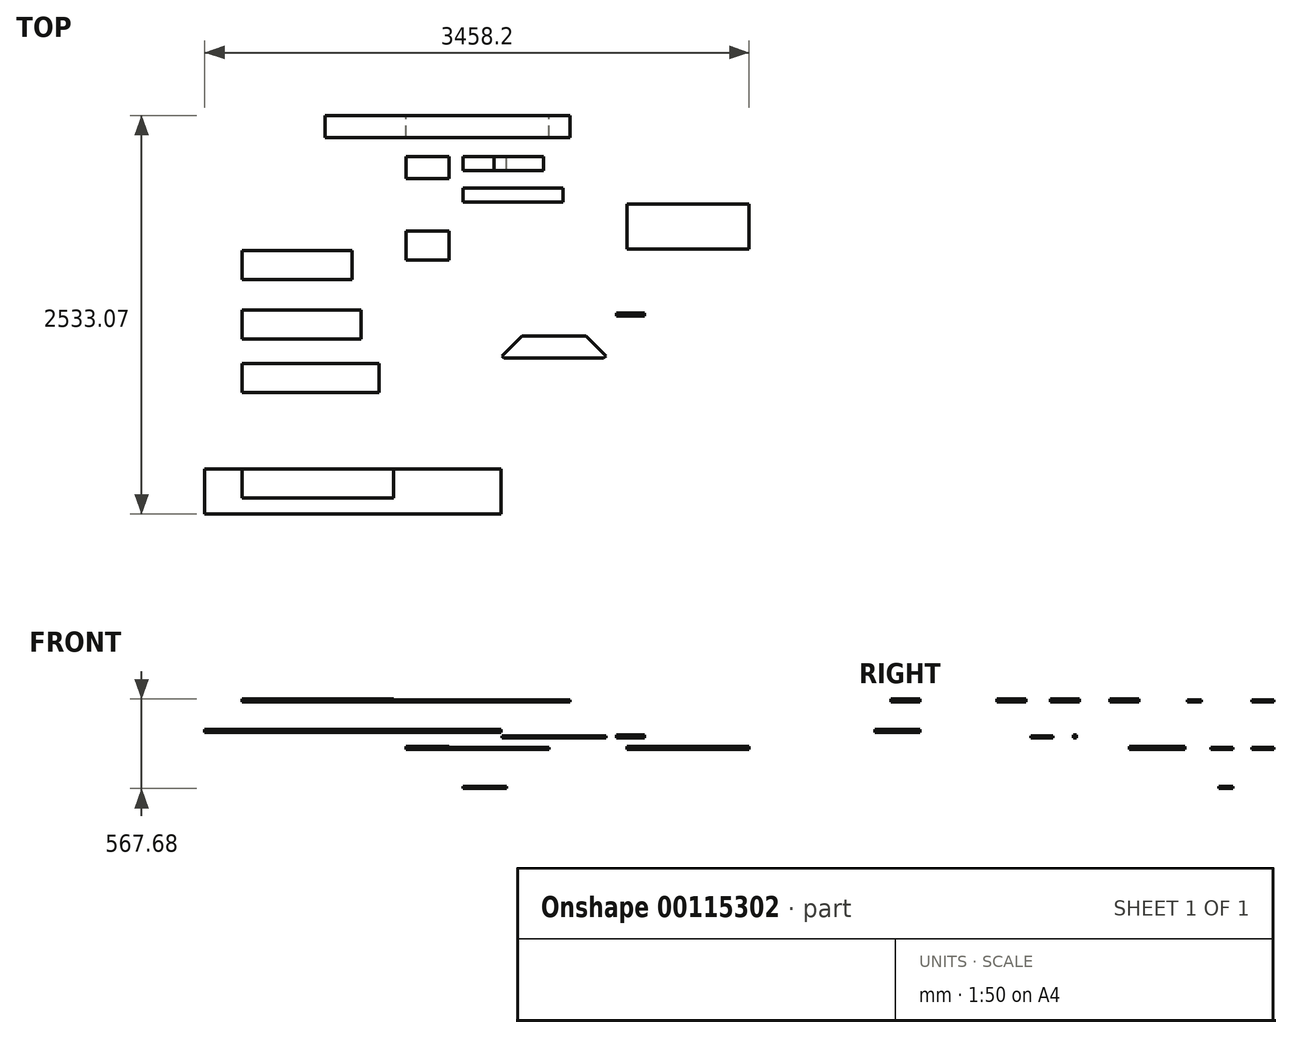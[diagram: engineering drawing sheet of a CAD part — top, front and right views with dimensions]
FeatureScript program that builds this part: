
annotation { "Feature Type Name" : "Feature", "Feature Type Description" : "" }
export const myFeature = defineFeature(function(context is Context, id is Id, definition is map)
    precondition{}
    {
        {
            var Q0;
            Q0=qCreatedBy(makeId("Right.planeOp"),FACE);
            var sketch = newSketch(context, id + "F0", { "sketchPlane" : qUnion([Q0])});
            skLineSegment(sketch, "E0.bottom", {"start": v(-154.99, 55.8) * mm, "end": v(29.16, 55.8) * mm});
            skLineSegment(sketch, "E0.top", {"start": v(-154.99, 36.74) * mm, "end": v(29.16, 36.74) * mm});
            skLineSegment(sketch, "E0.left", {"start": v(-154.99, 55.8) * mm, "end": v(-154.99, 36.74) * mm});
            skLineSegment(sketch, "E0.right", {"start": v(29.16, 55.8) * mm, "end": v(29.16, 36.74) * mm});
            skSolve(sketch);
        }
        {
            var Q0;
            Q0=makeQuery(id+"F0.imprint","IMPRINT",FACE,{"disambiguationData":[TD([[makeQuery(id+"F0.imprint","IMPRINT",EDGE,{"derivedFrom":sQuery(id+"F0.wireOp",EDGE,"E0.bottom")}),-1.0]])]});
            extrude(context, id + "F1", {"entities" : qUnion([Q0]), "depth" : 965.2 * mm});
        }
        {
            var Q0;
            Q0=makeQuery(id+"F1.opExtrude","SWEPT_BODY",BODY,{"disambiguationData":[OSD([sQuery(id+"F0.wireOp",EDGE,"E0.bottom"),sQuery(id+"F0.wireOp",EDGE,"E0.top"),sQuery(id+"F0.wireOp",EDGE,"E0.left"),sQuery(id+"F0.wireOp",EDGE,"E0.right")])]});
            transform(context, id + "F2", {"entities" : qUnion([Q0]), "transformType" : TransformType.TRANSLATION_3D, "dx" : 311.4 * mm, "dy" : 0 * mm, "dz" : 190.77 * mm, "makeCopy" : true});
        }
        {
            var Q0;
            Q0=makeQuery(id+"F1.opExtrude","SWEPT_FACE",FACE,{"disambiguationData":[OSD([sQuery(id+"F0.wireOp",EDGE,"E0.left")])]});
            extrude(context, id + "F3", {"entities" : qUnion([Q0]), "operationType" : NewBodyOperationType.ADD, "depth" : 69.85 * mm});
        }
        {
            var Q0;
            Q0=makeQuery(id+"F3.opExtrude","CAP_FACE",FACE,{"disambiguationData":[OSD([sQuery(id+"F0.wireOp",EDGE,"E0.left")])],"isStart":false});
            extrude(context, id + "F4", {"entities" : qUnion([Q0]), "operationType" : NewBodyOperationType.ADD, "depth" : 31.75 * mm});
        }
        {
            var Q0;
            {var subQ0=sQuery(id+"F0.wireOp",EDGE,"E0.left");var subQ1=makeQuery(id+"F1.opExtrude","CAP_EDGE",EDGE,{"disambiguationData":[OSD([subQ0])],"isStart":false});Q0=makeQuery(id+"F4.boolean.opBoolean","MERGE",FACE,{"derivedFrom":[makeQuery(id+"F3.boolean.opBoolean","MERGE",FACE,{"derivedFrom":[makeQuery(id+"F1.opExtrude","CAP_FACE",FACE,{"disambiguationData":[OSD([sQuery(id+"F0.wireOp",EDGE,"E0.bottom"),sQuery(id+"F0.wireOp",EDGE,"E0.top"),subQ0,sQuery(id+"F0.wireOp",EDGE,"E0.right")])],"isStart":false}),makeQuery(id+"F3.opExtrude","SWEPT_FACE",FACE,{"disambiguationData":[OSD([subQ0]),TDD([subQ1])]})]}),makeQuery(id+"F4.opExtrude","SWEPT_FACE",FACE,{"disambiguationData":[OSD([subQ0]),TDD([makeQuery(id+"F3.opExtrude","CAP_EDGE",EDGE,{"disambiguationData":[OSD([subQ0]),TDD([subQ1])],"isStart":false})])]})]});}
            extrude(context, id + "F5", {"entities" : qUnion([Q0]), "operationType" : NewBodyOperationType.ADD, "depth" : 990.6 * mm});
        }
        {
            var Q0;
            Q0=makeQuery(id+"F2.opPattern","COPY",FACE,{"derivedFrom":makeQuery(id+"F1.opExtrude","CAP_FACE",FACE,{"disambiguationData":[OSD([sQuery(id+"F0.wireOp",EDGE,"E0.bottom"),sQuery(id+"F0.wireOp",EDGE,"E0.top"),sQuery(id+"F0.wireOp",EDGE,"E0.left"),sQuery(id+"F0.wireOp",EDGE,"E0.right")])],"isStart":false}),"instanceName":"1"});
            extrude(context, id + "F6", {"entities" : qUnion([Q0]), "operationType" : NewBodyOperationType.ADD, "depth" : 6.35 * mm});
        }
        {
            var Q0;
            Q0=makeQuery(id+"F2.opPattern","COPY",BODY,{"derivedFrom":makeQuery(id+"F1.opExtrude","SWEPT_BODY",BODY,{"disambiguationData":[OSD([sQuery(id+"F0.wireOp",EDGE,"E0.bottom"),sQuery(id+"F0.wireOp",EDGE,"E0.top"),sQuery(id+"F0.wireOp",EDGE,"E0.left"),sQuery(id+"F0.wireOp",EDGE,"E0.right")])]}),"instanceName":"1"});
            transform(context, id + "F7", {"entities" : qUnion([Q0]), "transformType" : TransformType.TRANSLATION_3D, "dx" : 0 * mm, "dy" : 672.72 * mm, "dz" : 0 * mm, "makeCopy" : true});
        }
        {
            var Q0;
            Q0=makeQuery(id+"F7.opPattern","COPY",FACE,{"derivedFrom":makeQuery(id+"F6.opExtrude","CAP_FACE",FACE,{"disambiguationData":[OSD([sQuery(id+"F0.wireOp",EDGE,"E0.bottom"),sQuery(id+"F0.wireOp",EDGE,"E0.top"),sQuery(id+"F0.wireOp",EDGE,"E0.left"),sQuery(id+"F0.wireOp",EDGE,"E0.right")])],"isStart":false}),"instanceName":"1"});
            extrude(context, id + "F8", {"entities" : qUnion([Q0]), "operationType" : NewBodyOperationType.ADD, "oppositeDirection" : true, "depth" : 127 * mm});
        }
        {
            var Q0;
            Q0=makeQuery(id+"F7.opPattern","COPY",FACE,{"derivedFrom":makeQuery(id+"F6.opExtrude","CAP_FACE",FACE,{"disambiguationData":[OSD([sQuery(id+"F0.wireOp",EDGE,"E0.bottom"),sQuery(id+"F0.wireOp",EDGE,"E0.top"),sQuery(id+"F0.wireOp",EDGE,"E0.left"),sQuery(id+"F0.wireOp",EDGE,"E0.right")])],"isStart":false}),"instanceName":"1"});
            extrude(context, id + "F9", {"entities" : qUnion([Q0]), "operationType" : NewBodyOperationType.ADD, "oppositeDirection" : true, "depth" : 127 * mm});
        }
        {
            var Q0;
            Q0=makeQuery(id+"F7.opPattern","COPY",FACE,{"derivedFrom":makeQuery(id+"F6.opExtrude","CAP_FACE",FACE,{"disambiguationData":[OSD([sQuery(id+"F0.wireOp",EDGE,"E0.bottom"),sQuery(id+"F0.wireOp",EDGE,"E0.top"),sQuery(id+"F0.wireOp",EDGE,"E0.left"),sQuery(id+"F0.wireOp",EDGE,"E0.right")])],"isStart":false}),"instanceName":"1"});
            extrude(context, id + "F10", {"entities" : qUnion([Q0]), "operationType" : NewBodyOperationType.REMOVE, "oppositeDirection" : true, "depth" : 127 * mm});
        }
        {
            var Q0;
            Q0=makeQuery(id+"F7.opPattern","COPY",BODY,{"derivedFrom":makeQuery(id+"F2.opPattern","COPY",BODY,{"derivedFrom":makeQuery(id+"F1.opExtrude","SWEPT_BODY",BODY,{"disambiguationData":[OSD([sQuery(id+"F0.wireOp",EDGE,"E0.bottom"),sQuery(id+"F0.wireOp",EDGE,"E0.top"),sQuery(id+"F0.wireOp",EDGE,"E0.left"),sQuery(id+"F0.wireOp",EDGE,"E0.right")])]}),"instanceName":"1"}),"instanceName":"1"});
            transform(context, id + "F11", {"entities" : qUnion([Q0]), "transformType" : TransformType.TRANSLATION_3D, "dx" : 0 * mm, "dy" : 339.34 * mm, "dz" : 0 * mm, "makeCopy" : true});
        }
        {
            var Q0;
            Q0=makeQuery(id+"F11.opPattern","COPY",FACE,{"derivedFrom":makeQuery(id+"F10.boolean.opBoolean","COPY",FACE,{"derivedFrom":makeQuery(id+"F10.opExtrude","CAP_FACE",FACE,{"disambiguationData":[OSD([sQuery(id+"F0.wireOp",EDGE,"E0.bottom"),sQuery(id+"F0.wireOp",EDGE,"E0.top"),sQuery(id+"F0.wireOp",EDGE,"E0.left"),sQuery(id+"F0.wireOp",EDGE,"E0.right")])],"isStart":false})}),"instanceName":"1"});
            extrude(context, id + "F12", {"entities" : qUnion([Q0]), "operationType" : NewBodyOperationType.REMOVE, "oppositeDirection" : true, "depth" : 88.9 * mm});
        }
        {
            var Q0;
            Q0=makeQuery(id+"F11.opPattern","COPY",BODY,{"derivedFrom":makeQuery(id+"F7.opPattern","COPY",BODY,{"derivedFrom":makeQuery(id+"F2.opPattern","COPY",BODY,{"derivedFrom":makeQuery(id+"F1.opExtrude","SWEPT_BODY",BODY,{"disambiguationData":[OSD([sQuery(id+"F0.wireOp",EDGE,"E0.bottom"),sQuery(id+"F0.wireOp",EDGE,"E0.top"),sQuery(id+"F0.wireOp",EDGE,"E0.left"),sQuery(id+"F0.wireOp",EDGE,"E0.right")])]}),"instanceName":"1"}),"instanceName":"1"}),"instanceName":"1"});
            transform(context, id + "F13", {"entities" : qUnion([Q0]), "transformType" : TransformType.TRANSLATION_3D, "dx" : 0 * mm, "dy" : 376.5 * mm, "dz" : 0 * mm, "makeCopy" : true});
        }
        {
            var Q0;
            Q0=makeQuery(id+"F13.opPattern","COPY",FACE,{"derivedFrom":makeQuery(id+"F12.boolean.opBoolean","COPY",FACE,{"derivedFrom":makeQuery(id+"F12.opExtrude","CAP_FACE",FACE,{"disambiguationData":[OSD([sQuery(id+"F0.wireOp",EDGE,"E0.bottom"),sQuery(id+"F0.wireOp",EDGE,"E0.top"),sQuery(id+"F0.wireOp",EDGE,"E0.left"),sQuery(id+"F0.wireOp",EDGE,"E0.right")])],"isStart":false})}),"instanceName":"1"});
            extrude(context, id + "F14", {"entities" : qUnion([Q0]), "operationType" : NewBodyOperationType.REMOVE, "oppositeDirection" : true, "depth" : 57.15 * mm});
        }
        {
            var Q0;
            Q0=makeQuery(id+"F13.opPattern","COPY",BODY,{"derivedFrom":makeQuery(id+"F11.opPattern","COPY",BODY,{"derivedFrom":makeQuery(id+"F7.opPattern","COPY",BODY,{"derivedFrom":makeQuery(id+"F2.opPattern","COPY",BODY,{"derivedFrom":makeQuery(id+"F1.opExtrude","SWEPT_BODY",BODY,{"disambiguationData":[OSD([sQuery(id+"F0.wireOp",EDGE,"E0.bottom"),sQuery(id+"F0.wireOp",EDGE,"E0.top"),sQuery(id+"F0.wireOp",EDGE,"E0.left"),sQuery(id+"F0.wireOp",EDGE,"E0.right")])]}),"instanceName":"1"}),"instanceName":"1"}),"instanceName":"1"}),"instanceName":"1"});
            transform(context, id + "F15", {"entities" : qUnion([Q0]), "transformType" : TransformType.TRANSLATION_3D, "dx" : 1264.12 * mm, "dy" : 858.77 * mm, "dz" : 0 * mm, "makeCopy" : true});
        }
        {
            var Q0;
            {var subQ0=sQuery(id+"F0.wireOp",EDGE,"E0.bottom");Q0=makeQuery(id+"F15.opPattern","COPY",FACE,{"derivedFrom":makeQuery(id+"F13.opPattern","COPY",FACE,{"derivedFrom":makeQuery(id+"F11.opPattern","COPY",FACE,{"derivedFrom":makeQuery(id+"F7.opPattern","COPY",FACE,{"derivedFrom":makeQuery(id+"F6.boolean.opBoolean","MERGE",FACE,{"derivedFrom":[makeQuery(id+"F2.opPattern","COPY",FACE,{"derivedFrom":makeQuery(id+"F1.opExtrude","SWEPT_FACE",FACE,{"disambiguationData":[OSD([subQ0])]}),"instanceName":"1"}),makeQuery(id+"F6.opExtrude","SWEPT_FACE",FACE,{"disambiguationData":[OSD([subQ0])]})]}),"instanceName":"1"}),"instanceName":"1"}),"instanceName":"1"}),"instanceName":"1"});}
            extrude(context, id + "F16", {"entities" : qUnion([Q0]), "operationType" : NewBodyOperationType.REMOVE, "oppositeDirection" : true, "depth" : 6.35 * mm});
        }
        {
            var Q0;
            Q0=makeQuery(id+"F15.opPattern","COPY",FACE,{"derivedFrom":makeQuery(id+"F14.boolean.opBoolean","COPY",FACE,{"derivedFrom":makeQuery(id+"F14.opExtrude","CAP_FACE",FACE,{"disambiguationData":[OSD([sQuery(id+"F0.wireOp",EDGE,"E0.bottom"),sQuery(id+"F0.wireOp",EDGE,"E0.top"),sQuery(id+"F0.wireOp",EDGE,"E0.left"),sQuery(id+"F0.wireOp",EDGE,"E0.right")])],"isStart":false})}),"instanceName":"1"});
            extrude(context, id + "F17", {"entities" : qUnion([Q0]), "operationType" : NewBodyOperationType.ADD, "depth" : 6.35 * mm});
        }
        {
            var Q0;
            {var subQ0=sQuery(id+"F0.wireOp",EDGE,"E0.left");Q0=makeQuery(id+"F17.boolean.opBoolean","MERGE",FACE,{"derivedFrom":[makeQuery(id+"F15.opPattern","COPY",FACE,{"derivedFrom":makeQuery(id+"F13.opPattern","COPY",FACE,{"derivedFrom":makeQuery(id+"F11.opPattern","COPY",FACE,{"derivedFrom":makeQuery(id+"F7.opPattern","COPY",FACE,{"derivedFrom":makeQuery(id+"F6.boolean.opBoolean","MERGE",FACE,{"derivedFrom":[makeQuery(id+"F2.opPattern","COPY",FACE,{"derivedFrom":makeQuery(id+"F1.opExtrude","SWEPT_FACE",FACE,{"disambiguationData":[OSD([subQ0])]}),"instanceName":"1"}),makeQuery(id+"F6.opExtrude","SWEPT_FACE",FACE,{"disambiguationData":[OSD([subQ0])]})]}),"instanceName":"1"}),"instanceName":"1"}),"instanceName":"1"}),"instanceName":"1"}),makeQuery(id+"F17.opExtrude","SWEPT_FACE",FACE,{"disambiguationData":[OSD([subQ0])]})]});}
            extrude(context, id + "F18", {"entities" : qUnion([Q0]), "operationType" : NewBodyOperationType.REMOVE, "oppositeDirection" : true, "depth" : 44.45 * mm});
        }
        {
            var Q0;
            Q0=makeQuery(id+"F15.opPattern","COPY",BODY,{"derivedFrom":makeQuery(id+"F13.opPattern","COPY",BODY,{"derivedFrom":makeQuery(id+"F11.opPattern","COPY",BODY,{"derivedFrom":makeQuery(id+"F7.opPattern","COPY",BODY,{"derivedFrom":makeQuery(id+"F2.opPattern","COPY",BODY,{"derivedFrom":makeQuery(id+"F1.opExtrude","SWEPT_BODY",BODY,{"disambiguationData":[OSD([sQuery(id+"F0.wireOp",EDGE,"E0.bottom"),sQuery(id+"F0.wireOp",EDGE,"E0.top"),sQuery(id+"F0.wireOp",EDGE,"E0.left"),sQuery(id+"F0.wireOp",EDGE,"E0.right")])]}),"instanceName":"1"}),"instanceName":"1"}),"instanceName":"1"}),"instanceName":"1"}),"instanceName":"1"});
            transform(context, id + "F19", {"entities" : qUnion([Q0]), "transformType" : TransformType.TRANSLATION_3D, "dx" : 0 * mm, "dy" : -460.56 * mm, "dz" : 0 * mm, "makeCopy" : true});
        }
        {
            var Q0;
            Q0=makeQuery(id+"F19.opPattern","COPY",FACE,{"derivedFrom":makeQuery(id+"F18.boolean.opBoolean","COPY",FACE,{"derivedFrom":makeQuery(id+"F18.opExtrude","CAP_FACE",FACE,{"disambiguationData":[OSD([sQuery(id+"F0.wireOp",EDGE,"E0.left")])],"isStart":false})}),"instanceName":"1"});
            extrude(context, id + "F20", {"entities" : qUnion([Q0]), "operationType" : NewBodyOperationType.REMOVE, "oppositeDirection" : true, "depth" : 50.8 * mm});
        }
        {
            var Q0;
            Q0=makeQuery(id+"F19.opPattern","COPY",FACE,{"derivedFrom":makeQuery(id+"F17.opExtrude","CAP_FACE",FACE,{"disambiguationData":[OSD([sQuery(id+"F0.wireOp",EDGE,"E0.bottom"),sQuery(id+"F0.wireOp",EDGE,"E0.top"),sQuery(id+"F0.wireOp",EDGE,"E0.left"),sQuery(id+"F0.wireOp",EDGE,"E0.right")])],"isStart":false}),"instanceName":"1"});
            extrude(context, id + "F21", {"entities" : qUnion([Q0]), "operationType" : NewBodyOperationType.ADD, "depth" : 69.85 * mm});
        }
        {
            var Q0;
            Q0=makeQuery(id+"F15.opPattern","COPY",BODY,{"derivedFrom":makeQuery(id+"F13.opPattern","COPY",BODY,{"derivedFrom":makeQuery(id+"F11.opPattern","COPY",BODY,{"derivedFrom":makeQuery(id+"F7.opPattern","COPY",BODY,{"derivedFrom":makeQuery(id+"F2.opPattern","COPY",BODY,{"derivedFrom":makeQuery(id+"F1.opExtrude","SWEPT_BODY",BODY,{"disambiguationData":[OSD([sQuery(id+"F0.wireOp",EDGE,"E0.bottom"),sQuery(id+"F0.wireOp",EDGE,"E0.top"),sQuery(id+"F0.wireOp",EDGE,"E0.left"),sQuery(id+"F0.wireOp",EDGE,"E0.right")])]}),"instanceName":"1"}),"instanceName":"1"}),"instanceName":"1"}),"instanceName":"1"}),"instanceName":"1"});
            transform(context, id + "F22", {"entities" : qUnion([Q0]), "transformType" : TransformType.TRANSLATION_3D, "dx" : -225.1 * mm, "dy" : 0 * mm, "dz" : -300.24 * mm, "makeCopy" : true});
        }
        {
            var Q0;
            Q0=makeQuery(id+"F22.opPattern","COPY",FACE,{"derivedFrom":makeQuery(id+"F17.opExtrude","CAP_FACE",FACE,{"disambiguationData":[OSD([sQuery(id+"F0.wireOp",EDGE,"E0.bottom"),sQuery(id+"F0.wireOp",EDGE,"E0.top"),sQuery(id+"F0.wireOp",EDGE,"E0.left"),sQuery(id+"F0.wireOp",EDGE,"E0.right")])],"isStart":false}),"instanceName":"1"});
            extrude(context, id + "F23", {"entities" : qUnion([Q0]), "operationType" : NewBodyOperationType.ADD, "depth" : 177.8 * mm});
        }
        {
            var Q0;
            Q0=makeQuery(id+"F22.opPattern","COPY",BODY,{"derivedFrom":makeQuery(id+"F15.opPattern","COPY",BODY,{"derivedFrom":makeQuery(id+"F13.opPattern","COPY",BODY,{"derivedFrom":makeQuery(id+"F11.opPattern","COPY",BODY,{"derivedFrom":makeQuery(id+"F7.opPattern","COPY",BODY,{"derivedFrom":makeQuery(id+"F2.opPattern","COPY",BODY,{"derivedFrom":makeQuery(id+"F1.opExtrude","SWEPT_BODY",BODY,{"disambiguationData":[OSD([sQuery(id+"F0.wireOp",EDGE,"E0.bottom"),sQuery(id+"F0.wireOp",EDGE,"E0.top"),sQuery(id+"F0.wireOp",EDGE,"E0.left"),sQuery(id+"F0.wireOp",EDGE,"E0.right")])]}),"instanceName":"1"}),"instanceName":"1"}),"instanceName":"1"}),"instanceName":"1"}),"instanceName":"1"}),"instanceName":"1"});
            transform(context, id + "F24", {"entities" : qUnion([Q0]), "transformType" : TransformType.TRANSLATION_3D, "dx" : 0 * mm, "dy" : -261.53 * mm, "dz" : 0 * mm, "makeCopy" : true});
        }
        {
            var Q0;
            Q0=makeQuery(id+"F24.opPattern","COPY",FACE,{"derivedFrom":makeQuery(id+"F23.opExtrude","CAP_FACE",FACE,{"disambiguationData":[OSD([sQuery(id+"F0.wireOp",EDGE,"E0.bottom"),sQuery(id+"F0.wireOp",EDGE,"E0.top"),sQuery(id+"F0.wireOp",EDGE,"E0.left"),sQuery(id+"F0.wireOp",EDGE,"E0.right")])],"isStart":false}),"instanceName":"1"});
            extrude(context, id + "F25", {"entities" : qUnion([Q0]), "operationType" : NewBodyOperationType.REMOVE, "oppositeDirection" : true, "depth" : 577.85 * mm});
        }
        {
            var Q0;
            Q0=makeQuery(id+"F24.opPattern","COPY",BODY,{"derivedFrom":makeQuery(id+"F22.opPattern","COPY",BODY,{"derivedFrom":makeQuery(id+"F15.opPattern","COPY",BODY,{"derivedFrom":makeQuery(id+"F13.opPattern","COPY",BODY,{"derivedFrom":makeQuery(id+"F11.opPattern","COPY",BODY,{"derivedFrom":makeQuery(id+"F7.opPattern","COPY",BODY,{"derivedFrom":makeQuery(id+"F2.opPattern","COPY",BODY,{"derivedFrom":makeQuery(id+"F1.opExtrude","SWEPT_BODY",BODY,{"disambiguationData":[OSD([sQuery(id+"F0.wireOp",EDGE,"E0.bottom"),sQuery(id+"F0.wireOp",EDGE,"E0.top"),sQuery(id+"F0.wireOp",EDGE,"E0.left"),sQuery(id+"F0.wireOp",EDGE,"E0.right")])]}),"instanceName":"1"}),"instanceName":"1"}),"instanceName":"1"}),"instanceName":"1"}),"instanceName":"1"}),"instanceName":"1"}),"instanceName":"1"});
            transform(context, id + "F26", {"entities" : qUnion([Q0]), "transformType" : TransformType.TRANSLATION_3D, "dx" : 558.93 * mm, "dy" : 0 * mm, "dz" : 0 * mm, "makeCopy" : true});
        }
        {
            var Q0;
            {var subQ0=sQuery(id+"F0.wireOp",EDGE,"E0.left");Q0=makeQuery(id+"F26.opPattern","COPY",FACE,{"derivedFrom":makeQuery(id+"F24.opPattern","COPY",FACE,{"derivedFrom":makeQuery(id+"F23.boolean.opBoolean","MERGE",FACE,{"derivedFrom":[makeQuery(id+"F22.opPattern","COPY",FACE,{"derivedFrom":makeQuery(id+"F18.boolean.opBoolean","COPY",FACE,{"derivedFrom":makeQuery(id+"F18.opExtrude","CAP_FACE",FACE,{"disambiguationData":[OSD([subQ0])],"isStart":false})}),"instanceName":"1"}),makeQuery(id+"F23.opExtrude","SWEPT_FACE",FACE,{"disambiguationData":[OSD([subQ0])]})]}),"instanceName":"1"}),"instanceName":"1"});}
            extrude(context, id + "F27", {"entities" : qUnion([Q0]), "operationType" : NewBodyOperationType.REMOVE, "oppositeDirection" : true, "depth" : 50.8 * mm});
        }
        {
            var Q0;
            Q0=makeQuery(id+"F24.opPattern","COPY",BODY,{"derivedFrom":makeQuery(id+"F22.opPattern","COPY",BODY,{"derivedFrom":makeQuery(id+"F15.opPattern","COPY",BODY,{"derivedFrom":makeQuery(id+"F13.opPattern","COPY",BODY,{"derivedFrom":makeQuery(id+"F11.opPattern","COPY",BODY,{"derivedFrom":makeQuery(id+"F7.opPattern","COPY",BODY,{"derivedFrom":makeQuery(id+"F2.opPattern","COPY",BODY,{"derivedFrom":makeQuery(id+"F1.opExtrude","SWEPT_BODY",BODY,{"disambiguationData":[OSD([sQuery(id+"F0.wireOp",EDGE,"E0.bottom"),sQuery(id+"F0.wireOp",EDGE,"E0.top"),sQuery(id+"F0.wireOp",EDGE,"E0.left"),sQuery(id+"F0.wireOp",EDGE,"E0.right")])]}),"instanceName":"1"}),"instanceName":"1"}),"instanceName":"1"}),"instanceName":"1"}),"instanceName":"1"}),"instanceName":"1"}),"instanceName":"1"});
            transform(context, id + "F28", {"entities" : qUnion([Q0]), "transformType" : TransformType.TRANSLATION_3D, "dx" : 0 * mm, "dy" : -473.28 * mm, "dz" : 0 * mm, "makeCopy" : true});
        }
        {
            var Q0;
            {var subQ0=sQuery(id+"F0.wireOp",EDGE,"E0.left");Q0=makeQuery(id+"F28.opPattern","COPY",FACE,{"derivedFrom":makeQuery(id+"F24.opPattern","COPY",FACE,{"derivedFrom":makeQuery(id+"F23.boolean.opBoolean","MERGE",FACE,{"derivedFrom":[makeQuery(id+"F22.opPattern","COPY",FACE,{"derivedFrom":makeQuery(id+"F18.boolean.opBoolean","COPY",FACE,{"derivedFrom":makeQuery(id+"F18.opExtrude","CAP_FACE",FACE,{"disambiguationData":[OSD([subQ0])],"isStart":false})}),"instanceName":"1"}),makeQuery(id+"F23.opExtrude","SWEPT_FACE",FACE,{"disambiguationData":[OSD([subQ0])]})]}),"instanceName":"1"}),"instanceName":"1"});}
            extrude(context, id + "F29", {"entities" : qUnion([Q0]), "operationType" : NewBodyOperationType.ADD, "depth" : 44.45 * mm});
        }
        {
            var Q0;
            {var subQ0=sQuery(id+"F0.wireOp",EDGE,"E0.left");Q0=makeQuery(id+"F29.boolean.opBoolean","MERGE",FACE,{"derivedFrom":[makeQuery(id+"F28.opPattern","COPY",FACE,{"derivedFrom":makeQuery(id+"F25.boolean.opBoolean","COPY",FACE,{"derivedFrom":makeQuery(id+"F25.opExtrude","CAP_FACE",FACE,{"disambiguationData":[OSD([sQuery(id+"F0.wireOp",EDGE,"E0.bottom"),sQuery(id+"F0.wireOp",EDGE,"E0.top"),subQ0,sQuery(id+"F0.wireOp",EDGE,"E0.right")])],"isStart":false})}),"instanceName":"1"}),makeQuery(id+"F29.opExtrude","SWEPT_FACE",FACE,{"disambiguationData":[OSD([subQ0]),TDD([makeQuery(id+"F28.opPattern","COPY",EDGE,{"derivedFrom":makeQuery(id+"F25.boolean.opBoolean","COPY",EDGE,{"derivedFrom":makeQuery(id+"F25.opExtrude","CAP_EDGE",EDGE,{"disambiguationData":[OSD([subQ0])],"isStart":false})}),"instanceName":"1"})])]})]});}
            extrude(context, id + "F30", {"entities" : qUnion([Q0]), "operationType" : NewBodyOperationType.REMOVE, "oppositeDirection" : true, "depth" : 38.1 * mm});
        }
        {
            var Q0;
            {var subQ0=sQuery(id+"F0.wireOp",EDGE,"E0.bottom");Q0=makeQuery(id+"F29.boolean.opBoolean","MERGE",FACE,{"derivedFrom":[makeQuery(id+"F28.opPattern","COPY",FACE,{"derivedFrom":makeQuery(id+"F24.opPattern","COPY",FACE,{"derivedFrom":makeQuery(id+"F23.boolean.opBoolean","MERGE",FACE,{"derivedFrom":[makeQuery(id+"F22.opPattern","COPY",FACE,{"derivedFrom":makeQuery(id+"F17.boolean.opBoolean","MERGE",FACE,{"derivedFrom":[makeQuery(id+"F16.boolean.opBoolean","COPY",FACE,{"derivedFrom":makeQuery(id+"F16.opExtrude","CAP_FACE",FACE,{"disambiguationData":[OSD([subQ0])],"isStart":false})}),makeQuery(id+"F17.opExtrude","SWEPT_FACE",FACE,{"disambiguationData":[OSD([subQ0])]})]}),"instanceName":"1"}),makeQuery(id+"F23.opExtrude","SWEPT_FACE",FACE,{"disambiguationData":[OSD([subQ0])]})]}),"instanceName":"1"}),"instanceName":"1"}),makeQuery(id+"F29.opExtrude","SWEPT_FACE",FACE,{"disambiguationData":[OSD([subQ0,sQuery(id+"F0.wireOp",EDGE,"E0.left")])]})]});}
            extrude(context, id + "F31", {"entities" : qUnion([Q0]), "operationType" : NewBodyOperationType.ADD, "depth" : 6.35 * mm});
        }
        {
            var Q0;
            Q0=makeQuery(id+"F6.opExtrude","CAP_FACE",FACE,{"disambiguationData":[OSD([sQuery(id+"F0.wireOp",EDGE,"E0.bottom"),sQuery(id+"F0.wireOp",EDGE,"E0.top"),sQuery(id+"F0.wireOp",EDGE,"E0.left"),sQuery(id+"F0.wireOp",EDGE,"E0.right")])],"isStart":false});
            extrude(context, id + "F32", {"entities" : qUnion([Q0]), "operationType" : NewBodyOperationType.REMOVE, "oppositeDirection" : true, "depth" : 25.4 * mm});
        }
        {
            var Q0;
            Q0=makeQuery(id+"F10.boolean.opBoolean","COPY",FACE,{"derivedFrom":makeQuery(id+"F10.opExtrude","CAP_FACE",FACE,{"disambiguationData":[OSD([sQuery(id+"F0.wireOp",EDGE,"E0.bottom"),sQuery(id+"F0.wireOp",EDGE,"E0.top"),sQuery(id+"F0.wireOp",EDGE,"E0.left"),sQuery(id+"F0.wireOp",EDGE,"E0.right")])],"isStart":false})});
            extrude(context, id + "F33", {"entities" : qUnion([Q0]), "operationType" : NewBodyOperationType.ADD, "depth" : 25.4 * mm});
        }
        {
            var Q0;
            Q0=makeQuery(id+"F23.opExtrude","CAP_FACE",FACE,{"disambiguationData":[OSD([sQuery(id+"F0.wireOp",EDGE,"E0.bottom"),sQuery(id+"F0.wireOp",EDGE,"E0.top"),sQuery(id+"F0.wireOp",EDGE,"E0.left"),sQuery(id+"F0.wireOp",EDGE,"E0.right")])],"isStart":false});
            extrude(context, id + "F34", {"entities" : qUnion([Q0]), "operationType" : NewBodyOperationType.ADD, "depth" : 25.4 * mm});
        }
        {
            var Q0;
            Q0=makeQuery(id+"F17.opExtrude","CAP_FACE",FACE,{"disambiguationData":[OSD([sQuery(id+"F0.wireOp",EDGE,"E0.bottom"),sQuery(id+"F0.wireOp",EDGE,"E0.top"),sQuery(id+"F0.wireOp",EDGE,"E0.left"),sQuery(id+"F0.wireOp",EDGE,"E0.right")])],"isStart":false});
            extrude(context, id + "F35", {"entities" : qUnion([Q0]), "operationType" : NewBodyOperationType.ADD, "depth" : 25.4 * mm});
        }
        {
            var Q0;
            Q0=makeQuery(id+"F32.boolean.opBoolean","COPY",FACE,{"derivedFrom":makeQuery(id+"F32.opExtrude","CAP_FACE",FACE,{"disambiguationData":[OSD([sQuery(id+"F0.wireOp",EDGE,"E0.bottom"),sQuery(id+"F0.wireOp",EDGE,"E0.top"),sQuery(id+"F0.wireOp",EDGE,"E0.left"),sQuery(id+"F0.wireOp",EDGE,"E0.right")])],"isStart":false})});
            extrude(context, id + "F36", {"entities" : qUnion([Q0]), "operationType" : NewBodyOperationType.ADD, "depth" : 15.88 * mm});
        }
        {
            var Q0;
            {var subQ0=sQuery(id+"F0.wireOp",EDGE,"E0.left");var subQ1=sQuery(id+"F0.wireOp",EDGE,"E0.bottom");Q0=makeQuery(id+"F31.boolean.opBoolean","MERGE",FACE,{"derivedFrom":[makeQuery(id+"F30.boolean.opBoolean","COPY",FACE,{"derivedFrom":makeQuery(id+"F30.opExtrude","CAP_FACE",FACE,{"disambiguationData":[OSD([subQ1,sQuery(id+"F0.wireOp",EDGE,"E0.top"),subQ0,sQuery(id+"F0.wireOp",EDGE,"E0.right")])],"isStart":false})}),makeQuery(id+"F31.opExtrude","SWEPT_FACE",FACE,{"disambiguationData":[OSD([subQ1,subQ0]),TDD([makeQuery(id+"F30.boolean.opBoolean","COPY",EDGE,{"derivedFrom":makeQuery(id+"F30.opExtrude","CAP_EDGE",EDGE,{"disambiguationData":[OSD([subQ1,subQ0])],"isStart":false})})])]})]});}
            extrude(context, id + "F37", {"entities" : qUnion([Q0]), "operationType" : NewBodyOperationType.ADD, "depth" : 9.52 * mm});
        }
        {
            var Q0;
            Q0=makeQuery(id+"F26.opPattern","COPY",FACE,{"derivedFrom":makeQuery(id+"F25.boolean.opBoolean","COPY",FACE,{"derivedFrom":makeQuery(id+"F25.opExtrude","CAP_FACE",FACE,{"disambiguationData":[OSD([sQuery(id+"F0.wireOp",EDGE,"E0.bottom"),sQuery(id+"F0.wireOp",EDGE,"E0.top"),sQuery(id+"F0.wireOp",EDGE,"E0.left"),sQuery(id+"F0.wireOp",EDGE,"E0.right")])],"isStart":false})}),"instanceName":"1"});
            extrude(context, id + "F38", {"entities" : qUnion([Q0]), "operationType" : NewBodyOperationType.ADD, "depth" : 9.52 * mm});
        }
        {
            var Q0;
            Q0=makeQuery(id+"F25.boolean.opBoolean","COPY",FACE,{"derivedFrom":makeQuery(id+"F25.opExtrude","CAP_FACE",FACE,{"disambiguationData":[OSD([sQuery(id+"F0.wireOp",EDGE,"E0.bottom"),sQuery(id+"F0.wireOp",EDGE,"E0.top"),sQuery(id+"F0.wireOp",EDGE,"E0.left"),sQuery(id+"F0.wireOp",EDGE,"E0.right")])],"isStart":false})});
            extrude(context, id + "F39", {"entities" : qUnion([Q0]), "operationType" : NewBodyOperationType.ADD, "depth" : 9.52 * mm});
        }
        {
            var Q0;
            {var subQ0=sQuery(id+"F0.wireOp",EDGE,"E0.left");var subQ1=makeQuery(id+"F1.opExtrude","CAP_EDGE",EDGE,{"disambiguationData":[OSD([subQ0])],"isStart":true});Q0=makeQuery(id+"F4.boolean.opBoolean","MERGE",FACE,{"derivedFrom":[makeQuery(id+"F3.boolean.opBoolean","MERGE",FACE,{"derivedFrom":[makeQuery(id+"F1.opExtrude","CAP_FACE",FACE,{"disambiguationData":[OSD([sQuery(id+"F0.wireOp",EDGE,"E0.bottom"),sQuery(id+"F0.wireOp",EDGE,"E0.top"),subQ0,sQuery(id+"F0.wireOp",EDGE,"E0.right")])],"isStart":true}),makeQuery(id+"F3.opExtrude","SWEPT_FACE",FACE,{"disambiguationData":[OSD([subQ0]),TDD([subQ1])]})]}),makeQuery(id+"F4.opExtrude","SWEPT_FACE",FACE,{"disambiguationData":[OSD([subQ0]),TDD([makeQuery(id+"F3.opExtrude","CAP_EDGE",EDGE,{"disambiguationData":[OSD([subQ0]),TDD([subQ1])],"isStart":false})])]})]});}
            extrude(context, id + "F40", {"entities" : qUnion([Q0]), "operationType" : NewBodyOperationType.REMOVE, "oppositeDirection" : true, "depth" : 92.07 * mm});
        }
        {
            var Q0;
            Q0=makeQuery(id+"F40.boolean.opBoolean","COPY",FACE,{"derivedFrom":makeQuery(id+"F40.opExtrude","CAP_FACE",FACE,{"disambiguationData":[OSD([sQuery(id+"F0.wireOp",EDGE,"E0.bottom"),sQuery(id+"F0.wireOp",EDGE,"E0.top"),sQuery(id+"F0.wireOp",EDGE,"E0.left"),sQuery(id+"F0.wireOp",EDGE,"E0.right")])],"isStart":false})});
            extrude(context, id + "F41", {"entities" : qUnion([Q0]), "operationType" : NewBodyOperationType.ADD, "depth" : 19.05 * mm});
        }
        {
            var Q0;
            Q0=makeQuery(id+"F39.opExtrude","CAP_FACE",FACE,{"disambiguationData":[OSD([sQuery(id+"F0.wireOp",EDGE,"E0.bottom"),sQuery(id+"F0.wireOp",EDGE,"E0.top"),sQuery(id+"F0.wireOp",EDGE,"E0.left"),sQuery(id+"F0.wireOp",EDGE,"E0.right")])],"isStart":false});
            extrude(context, id + "F42", {"entities" : qUnion([Q0]), "operationType" : NewBodyOperationType.REMOVE, "oppositeDirection" : true, "depth" : 38.1 * mm});
        }
        {
            var Q0;
            Q0=makeQuery(id+"F26.opPattern","COPY",BODY,{"derivedFrom":makeQuery(id+"F24.opPattern","COPY",BODY,{"derivedFrom":makeQuery(id+"F22.opPattern","COPY",BODY,{"derivedFrom":makeQuery(id+"F15.opPattern","COPY",BODY,{"derivedFrom":makeQuery(id+"F13.opPattern","COPY",BODY,{"derivedFrom":makeQuery(id+"F11.opPattern","COPY",BODY,{"derivedFrom":makeQuery(id+"F7.opPattern","COPY",BODY,{"derivedFrom":makeQuery(id+"F2.opPattern","COPY",BODY,{"derivedFrom":makeQuery(id+"F1.opExtrude","SWEPT_BODY",BODY,{"disambiguationData":[OSD([sQuery(id+"F0.wireOp",EDGE,"E0.bottom"),sQuery(id+"F0.wireOp",EDGE,"E0.top"),sQuery(id+"F0.wireOp",EDGE,"E0.left"),sQuery(id+"F0.wireOp",EDGE,"E0.right")])]}),"instanceName":"1"}),"instanceName":"1"}),"instanceName":"1"}),"instanceName":"1"}),"instanceName":"1"}),"instanceName":"1"}),"instanceName":"1"}),"instanceName":"1"});
            transform(context, id + "F43", {"entities" : qUnion([Q0]), "transformType" : TransformType.TRANSLATION_3D, "dx" : -194.44 * mm, "dy" : 0 * mm, "dz" : -248.4 * mm, "makeCopy" : true});
        }
        {
            var Q0;
            Q0=makeQuery(id+"F43.opPattern","COPY",FACE,{"derivedFrom":makeQuery(id+"F38.opExtrude","CAP_FACE",FACE,{"disambiguationData":[OSD([sQuery(id+"F0.wireOp",EDGE,"E0.bottom"),sQuery(id+"F0.wireOp",EDGE,"E0.top"),sQuery(id+"F0.wireOp",EDGE,"E0.left"),sQuery(id+"F0.wireOp",EDGE,"E0.right")])],"isStart":false}),"instanceName":"1"});
            extrude(context, id + "F44", {"entities" : qUnion([Q0]), "operationType" : NewBodyOperationType.REMOVE, "oppositeDirection" : true, "depth" : 38.1 * mm});
        }
        {
            var Q0;
            Q0=qCreatedBy(makeId("Top.planeOp"),FACE);
            var sketch = newSketch(context, id + "F45", { "sketchPlane" : qUnion([Q0])});
            skLineSegment(sketch, "E1", {"start": v(1948.51, 734) * mm, "end": v(1975.45, 734) * mm, "construction": true});
            skLineSegment(sketch, "E2", {"start": v(2634.31, 734) * mm, "end": v(2620.84, 747.46) * mm, "construction": true});
            skLineSegment(sketch, "E3", {"start": v(2494.61, 873.7) * mm, "end": v(2088.21, 873.7) * mm});
            skLineSegment(sketch, "E4", {"start": v(2088.21, 873.7) * mm, "end": v(1961.98, 747.46) * mm});
            skLineSegment(sketch, "E5.bottom", {"start": v(2689.77, 1021.9) * mm, "end": v(2918.37, 1021.9) * mm});
            skLineSegment(sketch, "E5.top", {"start": v(2689.77, 1002.84) * mm, "end": v(2918.37, 1002.84) * mm});
            skLineSegment(sketch, "E5.left", {"start": v(2689.77, 1021.9) * mm, "end": v(2689.77, 1002.84) * mm});
            skLineSegment(sketch, "E5.right", {"start": v(2918.37, 1021.9) * mm, "end": v(2918.37, 1002.84) * mm});
            skLineSegment(sketch, "E6", {"start": v(1961.98, 747.46) * mm, "end": v(1975.45, 734) * mm});
            skLineSegment(sketch, "E7", {"start": v(2620.84, 747.46) * mm, "end": v(2607.37, 734) * mm});
            skLineSegment(sketch, "E8", {"start": v(1975.45, 734) * mm, "end": v(2607.37, 734) * mm});
            skLineSegment(sketch, "E9", {"start": v(1961.98, 747.46) * mm, "end": v(1948.51, 734) * mm, "construction": true});
            skLineSegment(sketch, "E10", {"start": v(2607.37, 734) * mm, "end": v(2634.31, 734) * mm, "construction": true});
            skLineSegment(sketch, "E11", {"start": v(2620.84, 747.46) * mm, "end": v(2494.61, 873.7) * mm});
            skSolve(sketch);
        }
        {
            var Q0;
            Q0=makeQuery(id+"F45.imprint","IMPRINT",FACE,{"disambiguationData":[TD([[makeQuery(id+"F45.imprint","IMPRINT",EDGE,{"derivedFrom":sQuery(id+"F45.wireOp",EDGE,"E5.bottom")}),-1.0]])]});
            extrude(context, id + "F46", {"entities" : qUnion([Q0]), "depth" : 19.05 * mm});
        }
        {
            var Q0;
            Q0=makeQuery(id+"F45.imprint","IMPRINT",FACE,{"disambiguationData":[TD([[makeQuery(id+"F45.imprint","IMPRINT",EDGE,{"derivedFrom":sQuery(id+"F45.wireOp",EDGE,"E3")}),1.0]])]});
            extrude(context, id + "F47", {"entities" : qUnion([Q0]), "depth" : 12.7 * mm});
        }
        {
            var Q0;
            Q0=makeQuery(id+"F28.opPattern","COPY",BODY,{"derivedFrom":makeQuery(id+"F24.opPattern","COPY",BODY,{"derivedFrom":makeQuery(id+"F22.opPattern","COPY",BODY,{"derivedFrom":makeQuery(id+"F15.opPattern","COPY",BODY,{"derivedFrom":makeQuery(id+"F13.opPattern","COPY",BODY,{"derivedFrom":makeQuery(id+"F11.opPattern","COPY",BODY,{"derivedFrom":makeQuery(id+"F7.opPattern","COPY",BODY,{"derivedFrom":makeQuery(id+"F2.opPattern","COPY",BODY,{"derivedFrom":makeQuery(id+"F1.opExtrude","SWEPT_BODY",BODY,{"disambiguationData":[OSD([sQuery(id+"F0.wireOp",EDGE,"E0.bottom"),sQuery(id+"F0.wireOp",EDGE,"E0.top"),sQuery(id+"F0.wireOp",EDGE,"E0.left"),sQuery(id+"F0.wireOp",EDGE,"E0.right")])]}),"instanceName":"1"}),"instanceName":"1"}),"instanceName":"1"}),"instanceName":"1"}),"instanceName":"1"}),"instanceName":"1"}),"instanceName":"1"}),"instanceName":"1"});
            transform(context, id + "F48", {"entities" : qUnion([Q0]), "transformType" : TransformType.TRANSLATION_3D, "dx" : 1406.1 * mm, "dy" : 170.62 * mm, "dz" : 0 * mm, "makeCopy" : true});
        }
        {
            var Q0;
            Q0=makeQuery(id+"F48.opPattern","COPY",FACE,{"derivedFrom":makeQuery(id+"F37.opExtrude","CAP_FACE",FACE,{"disambiguationData":[OSD([sQuery(id+"F0.wireOp",EDGE,"E0.bottom"),sQuery(id+"F0.wireOp",EDGE,"E0.top"),sQuery(id+"F0.wireOp",EDGE,"E0.left"),sQuery(id+"F0.wireOp",EDGE,"E0.right")])],"isStart":false}),"instanceName":"1"});
            extrude(context, id + "F49", {"entities" : qUnion([Q0]), "operationType" : NewBodyOperationType.ADD, "depth" : 498.47 * mm});
        }
        {
            var Q0;
            {var subQ0=sQuery(id+"F0.wireOp",EDGE,"E0.left");var subQ1=sQuery(id+"F0.wireOp",EDGE,"E0.bottom");var subQ2=makeQuery(id+"F31.boolean.opBoolean","MERGE",EDGE,{"derivedFrom":[makeQuery(id+"F30.boolean.opBoolean","COPY",EDGE,{"derivedFrom":makeQuery(id+"F30.opExtrude","CAP_EDGE",EDGE,{"disambiguationData":[OSD([subQ0])],"isStart":false})}),makeQuery(id+"F31.opExtrude","SWEPT_EDGE",EDGE,{"disambiguationData":[OSD([subQ1,subQ0]),TDD([makeQuery(id+"F30.boolean.opBoolean","COPY",VERTEX,{"derivedFrom":makeQuery(id+"F30.opExtrude","CAP_VERTEX",VERTEX,{"disambiguationData":[OSD([subQ1,subQ0])],"isStart":false})})])]})]});Q0=makeQuery(id+"F49.boolean.opBoolean","MERGE",FACE,{"derivedFrom":[makeQuery(id+"F48.opPattern","COPY",FACE,{"derivedFrom":makeQuery(id+"F37.boolean.opBoolean","MERGE",FACE,{"derivedFrom":[makeQuery(id+"F31.boolean.opBoolean","MERGE",FACE,{"derivedFrom":[makeQuery(id+"F29.opExtrude","CAP_FACE",FACE,{"disambiguationData":[OSD([subQ0])],"isStart":false}),makeQuery(id+"F31.opExtrude","SWEPT_FACE",FACE,{"disambiguationData":[OSD([subQ1,subQ0]),TDD([makeQuery(id+"F29.opExtrude","CAP_EDGE",EDGE,{"disambiguationData":[OSD([subQ1,subQ0])],"isStart":false})])]})]}),makeQuery(id+"F37.opExtrude","SWEPT_FACE",FACE,{"disambiguationData":[OSD([subQ1,subQ0]),TDD([subQ2])]})]}),"instanceName":"1"}),makeQuery(id+"F49.opExtrude","SWEPT_FACE",FACE,{"disambiguationData":[OSD([subQ1,subQ0]),TDD([makeQuery(id+"F48.opPattern","COPY",EDGE,{"derivedFrom":makeQuery(id+"F37.opExtrude","CAP_EDGE",EDGE,{"disambiguationData":[OSD([subQ1,subQ0]),TDD([subQ2])],"isStart":false}),"instanceName":"1"})])]})]});}
            extrude(context, id + "F50", {"entities" : qUnion([Q0]), "operationType" : NewBodyOperationType.ADD, "depth" : 101.6 * mm});
        }
        {
            var Q0;
            Q0=makeQuery(id+"F46.opExtrude","SWEPT_FACE",FACE,{"disambiguationData":[OSD([sQuery(id+"F45.wireOp",EDGE,"E5.right")])]});
            extrude(context, id + "F51", {"entities" : qUnion([Q0]), "operationType" : NewBodyOperationType.REMOVE, "oppositeDirection" : true, "depth" : 50.8 * mm});
        }
        {
            var Q0;
            Q0=makeQuery(id+"F15.opPattern","COPY",FACE,{"derivedFrom":makeQuery(id+"F13.opPattern","COPY",FACE,{"derivedFrom":makeQuery(id+"F11.opPattern","COPY",FACE,{"derivedFrom":makeQuery(id+"F7.opPattern","COPY",FACE,{"derivedFrom":makeQuery(id+"F2.opPattern","COPY",FACE,{"derivedFrom":makeQuery(id+"F1.opExtrude","CAP_FACE",FACE,{"disambiguationData":[OSD([sQuery(id+"F0.wireOp",EDGE,"E0.bottom"),sQuery(id+"F0.wireOp",EDGE,"E0.top"),sQuery(id+"F0.wireOp",EDGE,"E0.left"),sQuery(id+"F0.wireOp",EDGE,"E0.right")])],"isStart":true}),"instanceName":"1"}),"instanceName":"1"}),"instanceName":"1"}),"instanceName":"1"}),"instanceName":"1"});
            extrude(context, id + "F52", {"entities" : qUnion([Q0]), "operationType" : NewBodyOperationType.ADD, "depth" : 800.1 * mm});
        }
        {
            var Q0;
            Q0=makeQuery(id+"F52.opExtrude","CAP_FACE",FACE,{"disambiguationData":[OSD([sQuery(id+"F0.wireOp",EDGE,"E0.bottom"),sQuery(id+"F0.wireOp",EDGE,"E0.top"),sQuery(id+"F0.wireOp",EDGE,"E0.left"),sQuery(id+"F0.wireOp",EDGE,"E0.right")])],"isStart":false});
            extrude(context, id + "F53", {"entities" : qUnion([Q0]), "operationType" : NewBodyOperationType.REMOVE, "oppositeDirection" : true, "depth" : 63.5 * mm});
        }
        {
            var Q0;
            Q0=makeQuery(id+"F19.opPattern","COPY",FACE,{"derivedFrom":makeQuery(id+"F15.opPattern","COPY",FACE,{"derivedFrom":makeQuery(id+"F13.opPattern","COPY",FACE,{"derivedFrom":makeQuery(id+"F11.opPattern","COPY",FACE,{"derivedFrom":makeQuery(id+"F7.opPattern","COPY",FACE,{"derivedFrom":makeQuery(id+"F2.opPattern","COPY",FACE,{"derivedFrom":makeQuery(id+"F1.opExtrude","CAP_FACE",FACE,{"disambiguationData":[OSD([sQuery(id+"F0.wireOp",EDGE,"E0.bottom"),sQuery(id+"F0.wireOp",EDGE,"E0.top"),sQuery(id+"F0.wireOp",EDGE,"E0.left"),sQuery(id+"F0.wireOp",EDGE,"E0.right")])],"isStart":true}),"instanceName":"1"}),"instanceName":"1"}),"instanceName":"1"}),"instanceName":"1"}),"instanceName":"1"}),"instanceName":"1"});
            extrude(context, id + "F54", {"entities" : qUnion([Q0]), "operationType" : NewBodyOperationType.REMOVE, "oppositeDirection" : true, "depth" : 139.7 * mm});
        }
        {
            var Q0;
            Q0=makeQuery(id+"F35.opExtrude","CAP_FACE",FACE,{"disambiguationData":[OSD([sQuery(id+"F0.wireOp",EDGE,"E0.bottom"),sQuery(id+"F0.wireOp",EDGE,"E0.top"),sQuery(id+"F0.wireOp",EDGE,"E0.left"),sQuery(id+"F0.wireOp",EDGE,"E0.right")])],"isStart":false});
            extrude(context, id + "F55", {"entities" : qUnion([Q0]), "operationType" : NewBodyOperationType.ADD, "depth" : 88.9 * mm});
        }
    });
